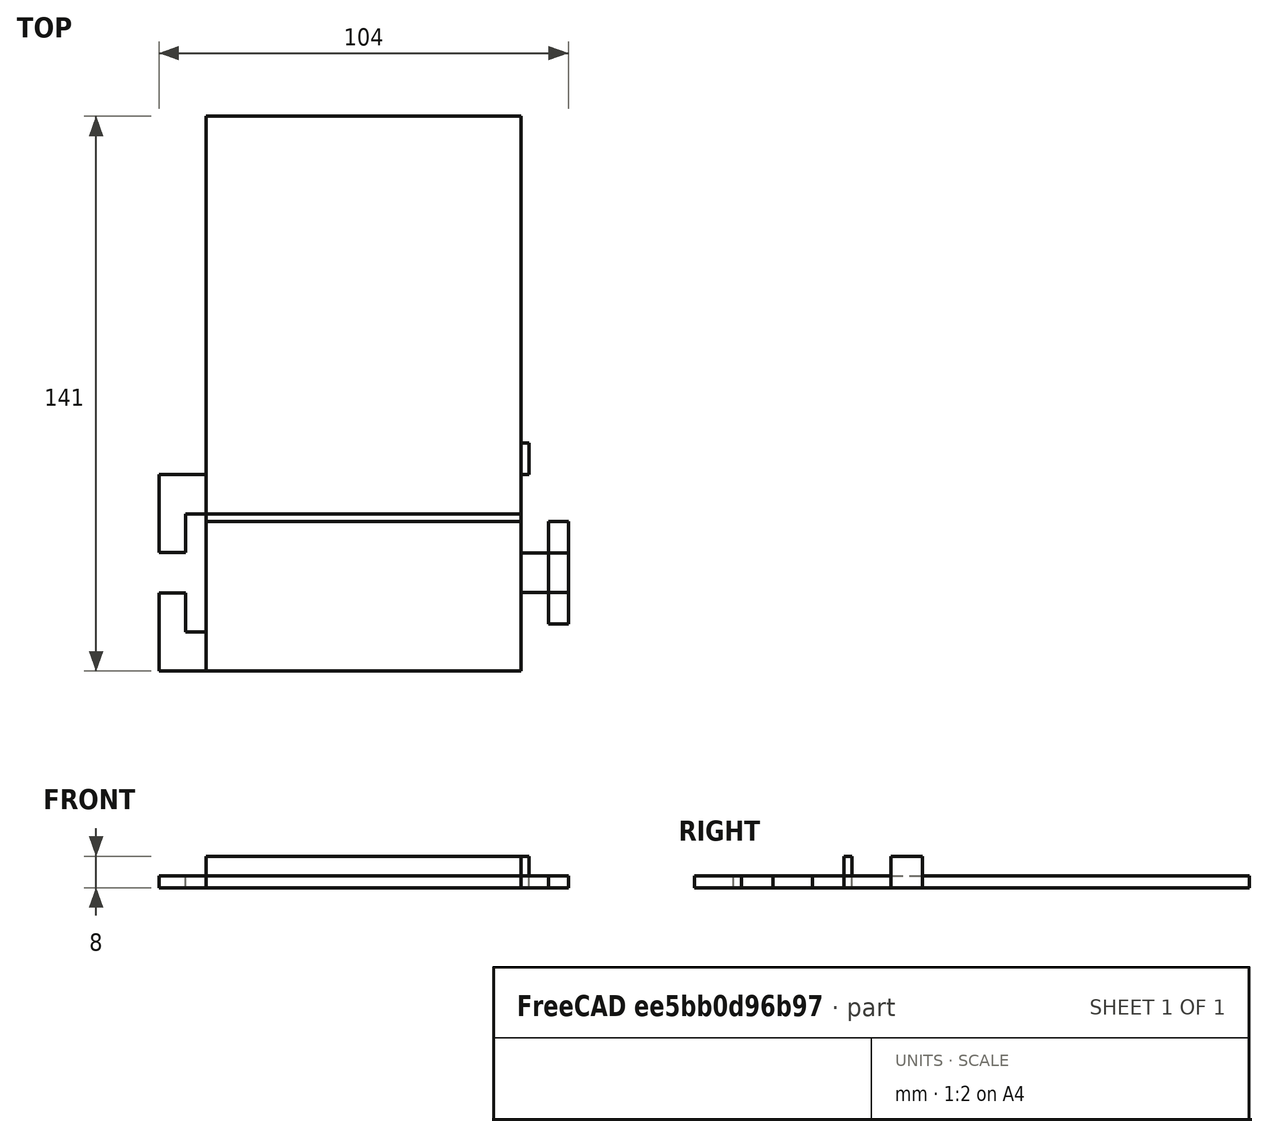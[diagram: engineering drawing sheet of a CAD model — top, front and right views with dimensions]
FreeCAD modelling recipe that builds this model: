
FCSTD DOCUMENT  (FreeCAD 0.21R33771 (Git))
Label: stand-tray
License: All rights reserved
LicenseURL: http://en.wikipedia.org/wiki/All_rights_reserved
objects: Part::Box×8, Part::Cut×2, Part::Mirroring×1
note: 11 computed .brp shape members not serialized (recipe doc carries the construction recipe); baked Part::Feature solids carry a one-line shape summary decoded from their .brp

FEATURE [Part::Box] Box  label="Cube"
  AttacherType = Attacher::AttachEngine3D
  Height = 3
  Length = 80
  Placement = pos=(-40,0,0) rot=(0,0,1;0rad)
  Width = 141
FEATURE [Part::Box] Box001  label="flansh"
  AttacherType = Attacher::AttachEngine3D
  Height = 3
  Length = 12
  Width = 50
FEATURE [Part::Box] Box002  label="nut-1"
  AttacherType = Attacher::AttachEngine3D
  Height = 3
  Length = 5.25
  Placement = pos=(6.75,10,0) rot=(0,0,1;0rad)
  Width = 30
FEATURE [Part::Box] Box003  label="nut-2"
  AttacherType = Attacher::AttachEngine3D
  Height = 4
  Length = 12
  Placement = pos=(0,19.9,0) rot=(0,0,1;0rad)
  Width = 10.2
FEATURE [Part::Cut] Cut
  Base = -> Box001
  Tool = -> Box002
FEATURE [Part::Cut] Cut001
  Base = -> Cut
  Placement = pos=(-52,0,0) rot=(0,0,1;0rad)
  Tool = -> Box003
FEATURE [Part::Box] Box004  label="right"
  AttacherType = Attacher::AttachEngine3D
  Height = 3
  Length = 12
  Placement = pos=(40,20,0) rot=(0,0,1;0rad)
  Width = 10
FEATURE [Part::Box] Box007  label="backstop"
  AttacherType = Attacher::AttachEngine3D
  Height = 5
  Length = 80
  Placement = pos=(-40,38,3) rot=(0,0,1;0rad)
  Width = 2
FEATURE [Part::Box] Box008  label="left-slide"
  AttacherType = Attacher::AttachEngine3D
  Height = 8
  Length = 2
  Placement = pos=(-42,50,0) rot=(0,0,1;0rad)
  Width = 8
FEATURE [Part::Box] Box010  label="Cube001"
  AttacherType = Attacher::AttachEngine3D
  Height = 3
  Length = 5
  Placement = pos=(47,12,0) rot=(0,0,1;0rad)
  Width = 26
FEATURE [Part::Mirroring] Part__Mirroring  label="left-slide (Mirror #1)"
  Base = (0,0,0)
  Normal = (1,0,0)
  Source = -> Box008
